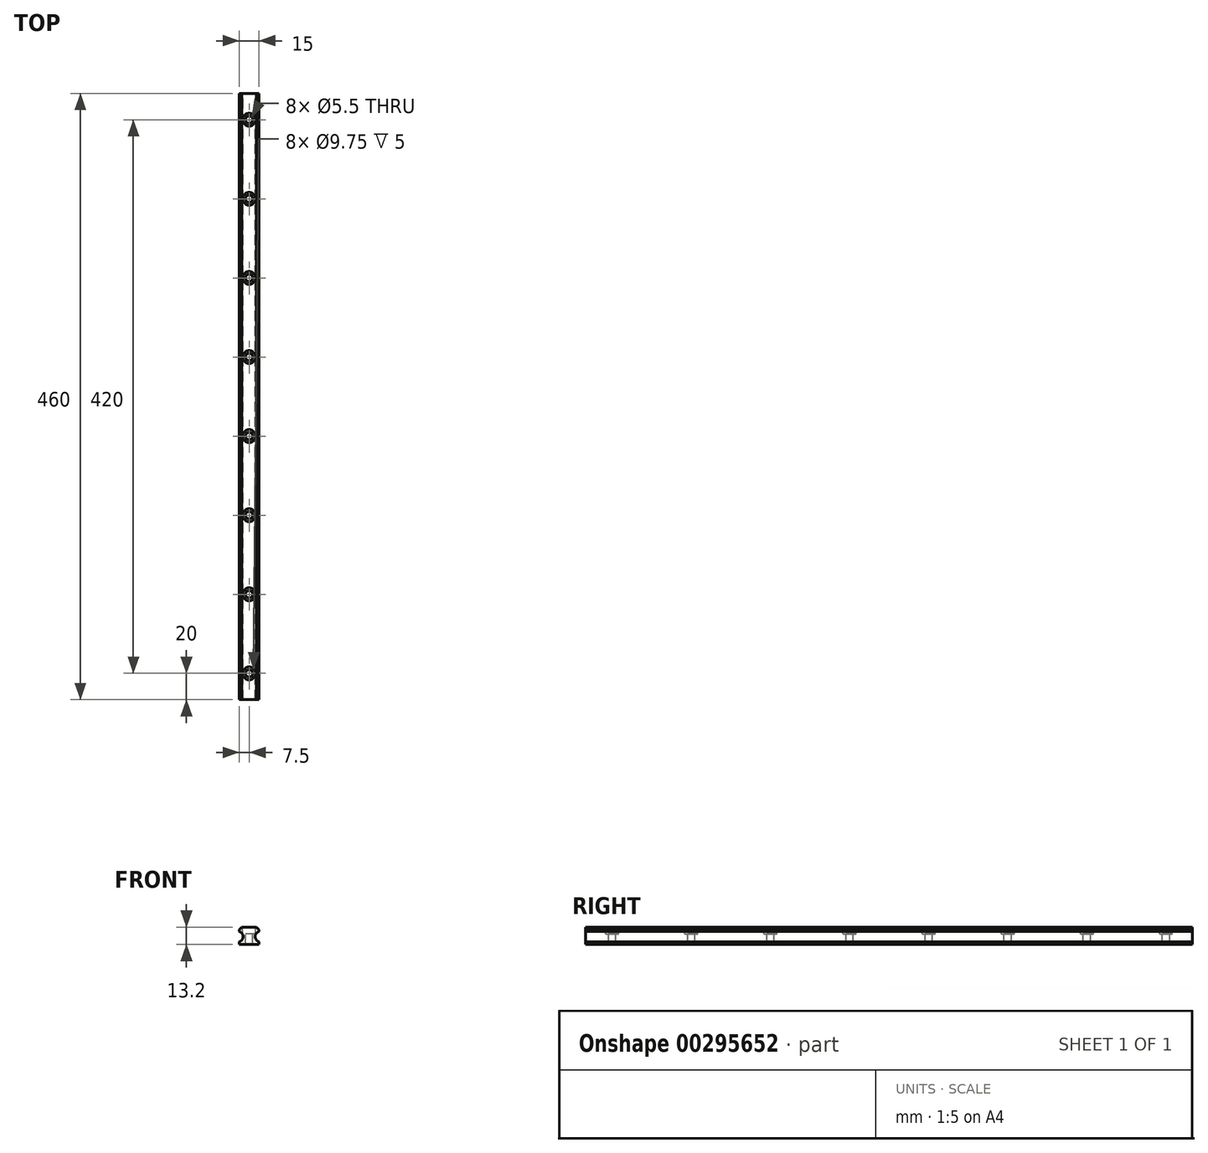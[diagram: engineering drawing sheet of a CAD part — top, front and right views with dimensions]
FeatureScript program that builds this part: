
annotation { "Feature Type Name" : "Feature", "Feature Type Description" : "" }
export const myFeature = defineFeature(function(context is Context, id is Id, definition is map)
    precondition{}
    {
        {
            var Q0;
            Q0=qCreatedBy(makeId("Front.planeOp"),FACE);
            var sketch = newSketch(context, id + "F0", { "sketchPlane" : qUnion([Q0])});
            skLineSegment(sketch, "E0", {"start": v(0, 0) * mm, "end": v(0, 42.87) * mm, "construction": true});
            skLineSegment(sketch, "E1.bottom", {"start": v(-7.5, 0) * mm, "end": v(7.5, 0) * mm});
            skLineSegment(sketch, "E1.top", {"start": v(-5.5, 13.2) * mm, "end": v(5.5, 13.2) * mm});
            skLineSegment(sketch, "E1.left", {"start": v(-7.5, 0) * mm, "end": v(-7.5, 2.15) * mm});
            skLineSegment(sketch, "E1.right", {"start": v(7.5, 0) * mm, "end": v(7.5, 2.15) * mm});
            skArc(sketch, "E2", {"start": v(-7.5, 2.15) * mm, "mid": v(-4.6, 6) * mm, "end": v(-7.5, 9.85) * mm});
            skArc(sketch, "E3", {"start": v(7.5, 9.85) * mm, "mid": v(4.6, 6) * mm, "end": v(7.5, 2.15) * mm});
            skLineSegment(sketch, "E4.trimOffspring", {"start": v(7.5, 9.85) * mm, "end": v(7.5, 11.2) * mm});
            skLineSegment(sketch, "E5.trimOffspring", {"start": v(-7.5, 9.85) * mm, "end": v(-7.5, 11.2) * mm});
            skLineSegment(sketch, "E6", {"start": v(-7.5, 11.2) * mm, "end": v(-5.5, 13.2) * mm});
            skLineSegment(sketch, "E7", {"start": v(5.5, 13.2) * mm, "end": v(7.5, 11.2) * mm});
            skSolve(sketch);
        }
        {
            var Q0;
            Q0 = qSketchRegion(id + "F0", true);
            extrude(context, id + "F1", {"entities" : qUnion([Q0]), "depth" : 460 * mm});
        }
        {
            var Q0;
            Q0=makeQuery(id+"F1.opExtrude","SWEPT_FACE",FACE,{"disambiguationData":[OSD([sQuery(id+"F0.wireOp",EDGE,"E1.top")])]});
            var sketch = newSketch(context, id + "F2", { "sketchPlane" : qUnion([Q0])});
            skLineSegment(sketch, "E8", {"start": v(0, 0) * mm, "end": v(0, -460) * mm, "construction": true});
            skPoint(sketch, "E9", {"position": v(0, -440) * mm});
            skPoint(sketch, "E10.0.1.0", {"position": v(0, -380) * mm});
            skPoint(sketch, "E10.0.2.0", {"position": v(0, -320) * mm});
            skPoint(sketch, "E10.0.3.0", {"position": v(0, -260) * mm});
            skPoint(sketch, "E10.0.4.0", {"position": v(0, -200) * mm});
            skPoint(sketch, "E10.0.5.0", {"position": v(0, -140) * mm});
            skPoint(sketch, "E10.0.6.0", {"position": v(0, -80) * mm});
            skPoint(sketch, "E10.0.7.0", {"position": v(0, -20) * mm});
            skLineSegment(sketch, "E10.direction1", {"start": v(0, -440) * mm, "end": v(25, -440) * mm, "construction": true});
            skLineSegment(sketch, "E10.direction2", {"start": v(0, -440) * mm, "end": v(0, -380) * mm, "construction": true});
            skSolve(sketch);
        }
        {
            var Q0;
            Q0=sQuery(id+"F2.wireOp",VERTEX,"E10.0.7.0");
            var Q1;
            Q1=sQuery(id+"F2.wireOp",VERTEX,"E10.0.6.0");
            var Q2;
            Q2=sQuery(id+"F2.wireOp",VERTEX,"E10.0.5.0");
            var Q3;
            Q3=sQuery(id+"F2.wireOp",VERTEX,"E10.0.4.0");
            var Q4;
            Q4=sQuery(id+"F2.wireOp",VERTEX,"E10.0.3.0");
            var Q5;
            Q5=sQuery(id+"F2.wireOp",VERTEX,"E10.0.2.0");
            var Q6;
            Q6=sQuery(id+"F2.wireOp",VERTEX,"E10.0.1.0");
            var Q7;
            Q7=sQuery(id+"F2.wireOp",VERTEX,"E9");
            var Q8;
            Q8=makeQuery(id+"F1.opExtrude","SWEPT_BODY",BODY,{"disambiguationData":[OSD([sQuery(id+"F0.wireOp",EDGE,"E1.bottom"),sQuery(id+"F0.wireOp",EDGE,"E1.top"),sQuery(id+"F0.wireOp",EDGE,"E1.left"),sQuery(id+"F0.wireOp",EDGE,"E1.right"),sQuery(id+"F0.wireOp",EDGE,"E2"),sQuery(id+"F0.wireOp",EDGE,"E3"),sQuery(id+"F0.wireOp",EDGE,"E4.trimOffspring"),sQuery(id+"F0.wireOp",EDGE,"E5.trimOffspring"),sQuery(id+"F0.wireOp",EDGE,"E6"),sQuery(id+"F0.wireOp",EDGE,"E7")])]});
            hole(context, id + "F3", {"style" : HoleStyle.C_BORE, "endStyle" : HoleEndStyle.THROUGH, "standardTappedOrClearance" : lookupTablePath({ "standard" : "ISO", "fit" : "Normal", "size" : "M5", "type" : "Clearance" }), "standardBlindInLast" : lookupTablePath({ "fit" : "Standard", "standard" : "ISO", "size" : "M5", "type" : "Clearance" }), "holeDiameter" : 5.5 * mm, "cBoreDiameter" : 9.75 * mm, "cBoreDepth" : 5 * mm, "tappedDepth" : 12 * mm, "tapClearance" : 3, "locations" : qUnion([Q0, Q1, Q2, Q3, Q4, Q5, Q6, Q7]), "scope" : qUnion([Q8])});
        }
    });
